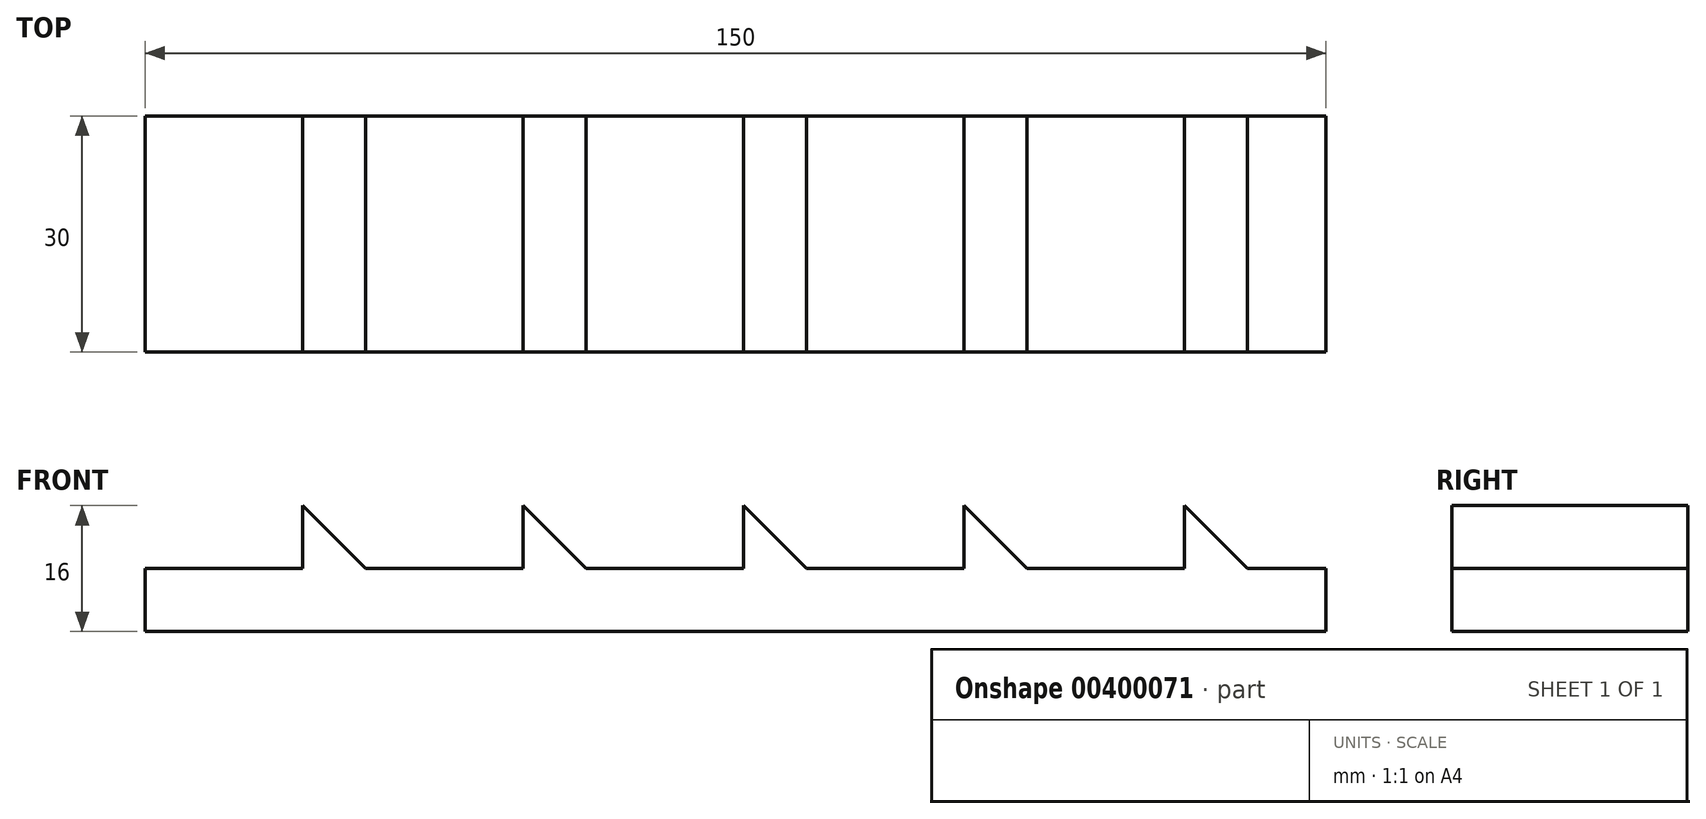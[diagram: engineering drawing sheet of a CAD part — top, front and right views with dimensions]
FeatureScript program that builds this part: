
annotation { "Feature Type Name" : "Feature", "Feature Type Description" : "" }
export const myFeature = defineFeature(function(context is Context, id is Id, definition is map)
    precondition{}
    {
        {
            var Q0;
            Q0=qCreatedBy(makeId("Top.planeOp"),FACE);
            var sketch = newSketch(context, id + "F0", { "sketchPlane" : qUnion([Q0])});
            skLineSegment(sketch, "E0.bottom", {"start": v(0, 0) * mm, "end": v(150, 0) * mm});
            skLineSegment(sketch, "E0.top", {"start": v(0, 30) * mm, "end": v(150, 30) * mm});
            skLineSegment(sketch, "E0.left", {"start": v(0, 0) * mm, "end": v(0, 30) * mm});
            skLineSegment(sketch, "E0.right", {"start": v(150, 0) * mm, "end": v(150, 30) * mm});
            skLineSegment(sketch, "E1", {"start": v(0, 18.53) * mm, "end": v(40, 18.53) * mm, "construction": true});
            skSolve(sketch);
        }
        {
            var Q0;
            Q0=qCreatedBy(makeId("Front.planeOp"),FACE);
            var sketch = newSketch(context, id + "F1", { "sketchPlane" : qUnion([Q0])});
            skLineSegment(sketch, "E2.bottom", {"start": v(0, 0) * mm, "end": v(150, 0) * mm});
            skLineSegment(sketch, "E2.top", {"start": v(0, 16) * mm, "end": v(150, 16) * mm});
            skLineSegment(sketch, "E2.left", {"start": v(0, 0) * mm, "end": v(0, 16) * mm});
            skLineSegment(sketch, "E2.right", {"start": v(150, 0) * mm, "end": v(150, 16) * mm});
            skLineSegment(sketch, "E3", {"start": v(0, 8) * mm, "end": v(20, 8) * mm, "construction": true});
            skLineSegment(sketch, "E4", {"start": v(20, 8) * mm, "end": v(20, 16) * mm});
            skLineSegment(sketch, "E5", {"start": v(20, 16) * mm, "end": v(28, 8) * mm});
            skLineSegment(sketch, "E6", {"start": v(28, 8) * mm, "end": v(20, 8) * mm});
            skLineSegment(sketch, "E7", {"start": v(28, 8) * mm, "end": v(48, 8) * mm, "construction": true});
            skLineSegment(sketch, "E8", {"start": v(48, 8) * mm, "end": v(56, 8) * mm, "construction": true});
            skLineSegment(sketch, "E9", {"start": v(56, 8) * mm, "end": v(76, 8) * mm, "construction": true});
            skLineSegment(sketch, "E10", {"start": v(76, 8) * mm, "end": v(84, 8) * mm, "construction": true});
            skLineSegment(sketch, "E11", {"start": v(84, 8) * mm, "end": v(104, 8) * mm, "construction": true});
            skLineSegment(sketch, "E12", {"start": v(104, 8) * mm, "end": v(112, 8) * mm, "construction": true});
            skLineSegment(sketch, "E13", {"start": v(112, 8) * mm, "end": v(132, 8) * mm, "construction": true});
            skLineSegment(sketch, "E14", {"start": v(132, 8) * mm, "end": v(140, 8) * mm, "construction": true});
            skLineSegment(sketch, "E15", {"start": v(140, 8) * mm, "end": v(150, 8) * mm, "construction": true});
            skLineSegment(sketch, "E16", {"start": v(48, 8) * mm, "end": v(48, 16) * mm});
            skLineSegment(sketch, "E17", {"start": v(48, 16) * mm, "end": v(56, 8) * mm});
            skLineSegment(sketch, "E18", {"start": v(48, 8) * mm, "end": v(56, 8) * mm});
            skLineSegment(sketch, "E19", {"start": v(76, 8) * mm, "end": v(76, 16) * mm});
            skLineSegment(sketch, "E20", {"start": v(76, 16) * mm, "end": v(84, 8) * mm});
            skLineSegment(sketch, "E21", {"start": v(76, 8) * mm, "end": v(84, 8) * mm});
            skLineSegment(sketch, "E22", {"start": v(104, 8) * mm, "end": v(104, 16) * mm});
            skLineSegment(sketch, "E23", {"start": v(104, 16) * mm, "end": v(112, 8) * mm});
            skLineSegment(sketch, "E24", {"start": v(104, 8) * mm, "end": v(112, 8) * mm});
            skLineSegment(sketch, "E25", {"start": v(132, 8) * mm, "end": v(132, 16) * mm});
            skLineSegment(sketch, "E26", {"start": v(132, 16) * mm, "end": v(140, 8) * mm});
            skLineSegment(sketch, "E27", {"start": v(132, 8) * mm, "end": v(140, 8) * mm});
            skSolve(sketch);
        }
        {
            var Q0;
            Q0=makeQuery(id+"F0.imprint","IMPRINT",FACE,{"disambiguationData":[TD([[makeQuery(id+"F0.imprint","IMPRINT",EDGE,{"derivedFrom":sQuery(id+"F0.wireOp",EDGE,"E0.bottom")}),1.0]])]});
            extrude(context, id + "F2", {"entities" : qUnion([Q0]), "depth" : 8 * mm});
        }
        {
            var Q0;
            Q0=makeQuery(id+"F1.imprint","IMPRINT",FACE,{"disambiguationData":[TD([[makeQuery(id+"F1.imprint","IMPRINT",EDGE,{"derivedFrom":sQuery(id+"F1.wireOp",EDGE,"E4")}),-1.0]])]});
            var Q1;
            Q1=makeQuery(id+"F1.imprint","IMPRINT",FACE,{"disambiguationData":[TD([[makeQuery(id+"F1.imprint","IMPRINT",EDGE,{"derivedFrom":sQuery(id+"F1.wireOp",EDGE,"E16")}),-1.0]])]});
            var Q2;
            Q2=makeQuery(id+"F1.imprint","IMPRINT",FACE,{"disambiguationData":[TD([[makeQuery(id+"F1.imprint","IMPRINT",EDGE,{"derivedFrom":sQuery(id+"F1.wireOp",EDGE,"E19")}),-1.0]])]});
            var Q3;
            Q3=makeQuery(id+"F1.imprint","IMPRINT",FACE,{"disambiguationData":[TD([[makeQuery(id+"F1.imprint","IMPRINT",EDGE,{"derivedFrom":sQuery(id+"F1.wireOp",EDGE,"E22")}),-1.0]])]});
            var Q4;
            Q4=makeQuery(id+"F1.imprint","IMPRINT",FACE,{"disambiguationData":[TD([[makeQuery(id+"F1.imprint","IMPRINT",EDGE,{"derivedFrom":sQuery(id+"F1.wireOp",EDGE,"E25")}),-1.0]])]});
            extrude(context, id + "F3", {"entities" : qUnion([Q0, Q1, Q2, Q3, Q4]), "operationType" : NewBodyOperationType.ADD, "oppositeDirection" : true, "depth" : 30 * mm});
        }
    });
